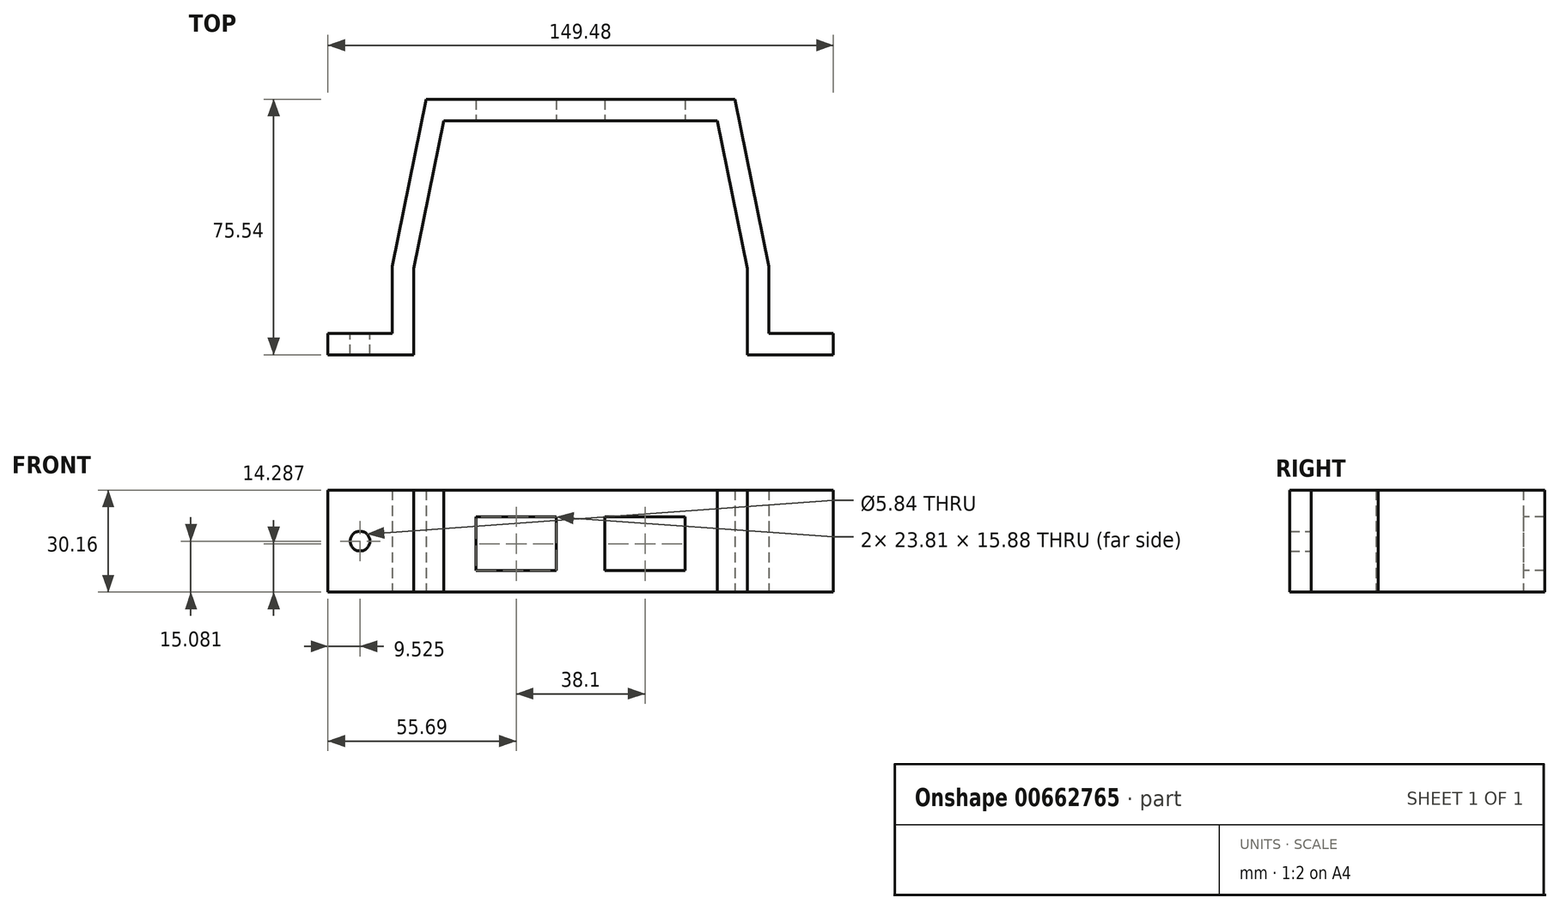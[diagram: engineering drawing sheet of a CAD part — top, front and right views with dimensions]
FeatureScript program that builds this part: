
annotation { "Feature Type Name" : "Feature", "Feature Type Description" : "" }
export const myFeature = defineFeature(function(context is Context, id is Id, definition is map)
    precondition{}
    {
        {
            var Q0;
            Q0=qCreatedBy(makeId("Top.planeOp"),FACE);
            var sketch = newSketch(context, id + "F0", { "sketchPlane" : qUnion([Q0])});
            skLineSegment(sketch, "E0", {"start": v(0, 0) * mm, "end": v(40.48, 0) * mm});
            skLineSegment(sketch, "E1", {"start": v(40.48, 0) * mm, "end": v(49.34, -43.66) * mm});
            skLineSegment(sketch, "E2", {"start": v(49.34, -43.66) * mm, "end": v(49.34, -69.19) * mm});
            skLineSegment(sketch, "E3", {"start": v(49.34, -69.19) * mm, "end": v(55.69, -69.19) * mm});
            skLineSegment(sketch, "E4", {"start": v(55.69, -43.02) * mm, "end": v(45.67, 6.35) * mm});
            skLineSegment(sketch, "E5", {"start": v(45.67, 6.35) * mm, "end": v(0, 6.35) * mm});
            skLineSegment(sketch, "E6", {"start": v(0, 6.35) * mm, "end": v(0, 0) * mm, "construction": true});
            skLineSegment(sketch, "E7", {"start": v(44.91, -21.83) * mm, "end": v(51.13, -20.57) * mm, "construction": true});
            skLineSegment(sketch, "E8", {"start": v(0, 61.38) * mm, "end": v(0, -75.9) * mm, "construction": true});
            skLineSegment(sketch, "E9.MirrorCS", {"start": v(-45.67, 6.35) * mm, "end": v(0, 6.35) * mm});
            skLineSegment(sketch, "E10.MirrorCS", {"start": v(0, 0) * mm, "end": v(-40.48, 0) * mm});
            skLineSegment(sketch, "E11.MirrorCS", {"start": v(-40.48, 0) * mm, "end": v(-49.34, -43.66) * mm});
            skLineSegment(sketch, "E12.MirrorCS", {"start": v(-55.69, -43.02) * mm, "end": v(-45.67, 6.35) * mm});
            skLineSegment(sketch, "E13.MirrorCS", {"start": v(-49.34, -43.66) * mm, "end": v(-49.34, -69.19) * mm});
            skLineSegment(sketch, "E14.MirrorCS", {"start": v(-49.34, -69.19) * mm, "end": v(-55.69, -69.19) * mm});
            skLineSegment(sketch, "E15", {"start": v(55.69, -62.84) * mm, "end": v(74.74, -62.84) * mm});
            skLineSegment(sketch, "E16", {"start": v(74.74, -62.84) * mm, "end": v(74.74, -69.19) * mm});
            skLineSegment(sketch, "E17", {"start": v(74.74, -69.19) * mm, "end": v(55.69, -69.19) * mm});
            skLineSegment(sketch, "E18", {"start": v(55.69, -62.84) * mm, "end": v(55.69, -43.02) * mm});
            skLineSegment(sketch, "E19.MirrorCS", {"start": v(-55.69, -62.84) * mm, "end": v(-74.74, -62.84) * mm});
            skLineSegment(sketch, "E20.MirrorCS", {"start": v(-55.69, -62.84) * mm, "end": v(-55.69, -43.02) * mm});
            skLineSegment(sketch, "E21.MirrorCS", {"start": v(-74.74, -62.84) * mm, "end": v(-74.74, -69.19) * mm});
            skLineSegment(sketch, "E22.MirrorCS", {"start": v(-74.74, -69.19) * mm, "end": v(-55.69, -69.19) * mm});
            skSolve(sketch);
        }
        {
            var Q0;
            Q0=makeQuery(id+"F0.imprint","IMPRINT",FACE,{"disambiguationData":[TD([[makeQuery(id+"F0.imprint","IMPRINT",EDGE,{"derivedFrom":sQuery(id+"F0.wireOp",EDGE,"E0")}),1.0]])]});
            extrude(context, id + "F1", {"entities" : qUnion([Q0]), "depth" : 30.16 * mm, "offsetDistance" : 25.4 * mm});
        }
        {
            var Q0;
            Q0=makeQuery(id+"F1.opExtrude","SWEPT_FACE",FACE,{"disambiguationData":[OSD([sQuery(id+"F0.wireOp",EDGE,"E0"),sQuery(id+"F0.wireOp",EDGE,"E10.MirrorCS")])]});
            var sketch = newSketch(context, id + "F2", { "sketchPlane" : qUnion([Q0])});
            skLineSegment(sketch, "E23.bottom", {"start": v(-30.96, 22.23) * mm, "end": v(-7.14, 22.23) * mm});
            skLineSegment(sketch, "E23.top", {"start": v(-30.96, 6.35) * mm, "end": v(-7.14, 6.35) * mm});
            skLineSegment(sketch, "E23.left", {"start": v(-30.96, 22.23) * mm, "end": v(-30.96, 6.35) * mm});
            skLineSegment(sketch, "E23.right", {"start": v(-7.14, 22.23) * mm, "end": v(-7.14, 6.35) * mm});
            skLineSegment(sketch, "E24", {"start": v(0, 49.86) * mm, "end": v(0, -36.03) * mm, "construction": true});
            skLineSegment(sketch, "E25.MirrorCS", {"start": v(7.14, 22.23) * mm, "end": v(7.14, 6.35) * mm});
            skLineSegment(sketch, "E26.MirrorCS", {"start": v(30.96, 22.23) * mm, "end": v(7.14, 22.23) * mm});
            skLineSegment(sketch, "E27.MirrorCS", {"start": v(30.96, 22.23) * mm, "end": v(30.96, 6.35) * mm});
            skLineSegment(sketch, "E28.MirrorCS", {"start": v(30.96, 6.35) * mm, "end": v(7.14, 6.35) * mm});
            skSolve(sketch);
        }
        {
            var Q0;
            Q0=makeQuery(id+"F2.imprint","IMPRINT",FACE,{"disambiguationData":[TD([[makeQuery(id+"F2.imprint","IMPRINT",EDGE,{"derivedFrom":sQuery(id+"F2.wireOp",EDGE,"E23.bottom")}),-1.0]])]});
            var Q1;
            Q1=makeQuery(id+"F2.imprint","IMPRINT",FACE,{"disambiguationData":[TD([[makeQuery(id+"F2.imprint","IMPRINT",EDGE,{"derivedFrom":sQuery(id+"F2.wireOp",EDGE,"E25.MirrorCS")}),1.0]])]});
            var Q2;
            Q2=makeQuery(id+"F1.opExtrude","SWEPT_FACE",FACE,{"disambiguationData":[OSD([sQuery(id+"F0.wireOp",EDGE,"E5"),sQuery(id+"F0.wireOp",EDGE,"E9.MirrorCS")])]});
            extrude(context, id + "F3", {"entities" : qUnion([Q0, Q1]), "operationType" : NewBodyOperationType.REMOVE, "endBound" : BoundingType.UP_TO_SURFACE, "oppositeDirection" : true, "depth" : 25.4 * mm, "endBoundEntityFace" : qUnion([Q2]), "offsetDistance" : 25.4 * mm});
        }
        {
            var Q0;
            Q0=makeQuery(id+"F1.opExtrude","SWEPT_FACE",FACE,{"disambiguationData":[OSD([sQuery(id+"F0.wireOp",EDGE,"E19.MirrorCS")])]});
            var sketch = newSketch(context, id + "F4", { "sketchPlane" : qUnion([Q0])});
            skCircle(sketch, "E29", {"center": v(65.21, 15.08) * mm, "radius": 2.92 * mm});
            skCircle(sketch, "E30.MirrorC", {"center": v(-65.21, 15.08) * mm, "radius": 2.92 * mm});
            skPoint(sketch, "E31", {"position": v(74.74, 15.08) * mm});
            skLineSegment(sketch, "E32", {"start": v(74.74, 15.08) * mm, "end": v(55.69, 15.08) * mm, "construction": true});
            skSolve(sketch);
        }
        {
            var Q0;
            Q0=makeQuery(id+"F4.imprint","IMPRINT",FACE,{"disambiguationData":[TD([[makeQuery(id+"F4.imprint","IMPRINT",EDGE,{"derivedFrom":sQuery(id+"F4.wireOp",EDGE,"E29")}),1.0]])]});
            var Q1;
            Q1=makeQuery(id+"F4.imprint","IMPRINT",FACE,{"disambiguationData":[TD([[makeQuery(id+"F4.imprint","IMPRINT",EDGE,{"derivedFrom":sQuery(id+"F4.wireOp",EDGE,"db0f49e6-4c6e-4caf-94a3-00be406392360.MirrorC")}),-1.0]])]});
            var Q2;
            Q2=makeQuery(id+"F4.imprint","IMPRINT",FACE,{"disambiguationData":[TD([[makeQuery(id+"F4.imprint","IMPRINT",EDGE,{"derivedFrom":sQuery(id+"F4.wireOp",EDGE,"12c46ef2-3faa-480c-ba95-c249fc22d7e00.MirrorC")}),1.0]])]});
            var Q3;
            Q3=makeQuery(id+"F4.imprint","IMPRINT",FACE,{"disambiguationData":[TD([[makeQuery(id+"F4.imprint","IMPRINT",EDGE,{"derivedFrom":sQuery(id+"F4.wireOp",EDGE,"E30.MirrorC")}),-1.0]])]});
            extrude(context, id + "F5", {"entities" : qUnion([Q0, Q1, Q2, Q3]), "operationType" : NewBodyOperationType.REMOVE, "endBound" : BoundingType.UP_TO_NEXT, "oppositeDirection" : true, "depth" : 25.4 * mm, "offsetDistance" : 25.4 * mm});
        }
    });
